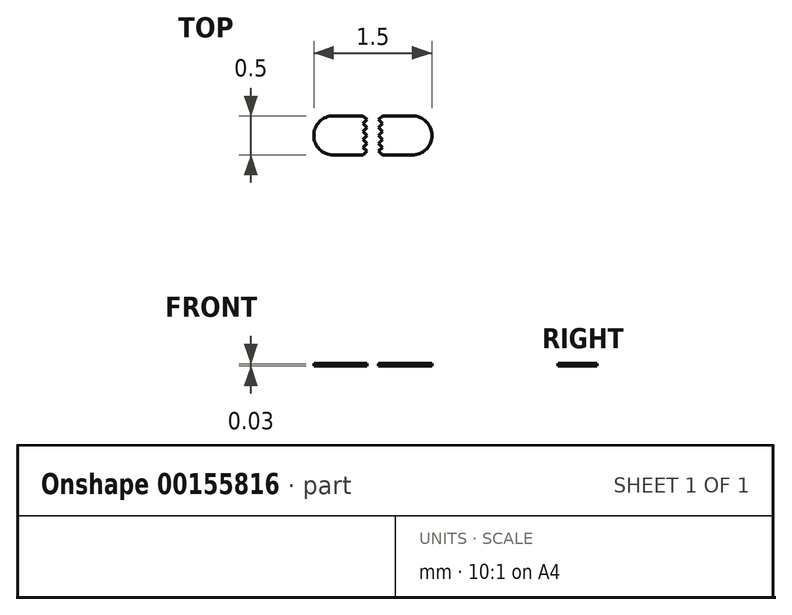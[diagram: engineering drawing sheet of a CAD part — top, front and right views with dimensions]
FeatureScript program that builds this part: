
annotation { "Feature Type Name" : "Feature", "Feature Type Description" : "" }
export const myFeature = defineFeature(function(context is Context, id is Id, definition is map)
    precondition{}
    {
        {
            var Q0;
            Q0=qCreatedBy(makeId("Top.planeOp"),FACE);
            var sketch = newSketch(context, id + "F0", { "sketchPlane" : qUnion([Q0])});
            skArc(sketch, "E0", {"start": v(-0.5, 0.25) * mm, "mid": v(-0.75, 0) * mm, "end": v(-0.5, -0.25) * mm});
            skLineSegment(sketch, "E1.bottom", {"start": v(-0.5, 0.25) * mm, "end": v(-0.13, 0.25) * mm});
            skLineSegment(sketch, "E1.top", {"start": v(-0.5, -0.25) * mm, "end": v(-0.12, -0.25) * mm});
            skLineSegment(sketch, "E2", {"start": v(-0.13, 0.25) * mm, "end": v(-0.08, 0.2) * mm});
            skLineSegment(sketch, "E3.MirrorCS", {"start": v(-0.13, 0.15) * mm, "end": v(-0.08, 0.2) * mm});
            skLineSegment(sketch, "E4.MirrorCS", {"start": v(-0.13, 0.15) * mm, "end": v(-0.08, 0.1) * mm});
            skLineSegment(sketch, "E5.MirrorCS", {"start": v(-0.13, 0.05) * mm, "end": v(-0.08, 0.1) * mm});
            skLineSegment(sketch, "E6", {"start": v(-0.12, 0.05) * mm, "end": v(-0.08, 0) * mm});
            skLineSegment(sketch, "E7.MirrorCS", {"start": v(-0.12, -0.05) * mm, "end": v(-0.08, 0) * mm});
            skLineSegment(sketch, "E8.MirrorCS", {"start": v(-0.13, -0.05) * mm, "end": v(-0.08, -0.1) * mm});
            skLineSegment(sketch, "E9.MirrorCS", {"start": v(-0.13, -0.15) * mm, "end": v(-0.08, -0.1) * mm});
            skLineSegment(sketch, "E10.MirrorCS", {"start": v(-0.13, -0.15) * mm, "end": v(-0.08, -0.2) * mm});
            skLineSegment(sketch, "E11.MirrorCS", {"start": v(-0.12, -0.25) * mm, "end": v(-0.07, -0.2) * mm});
            skPoint(sketch, "E12.center.orphan", {"position": v(0.5, 0) * mm});
            skLineSegment(sketch, "E13.MirrorCS", {"start": v(0.13, 0.05) * mm, "end": v(0.08, 0.1) * mm});
            skLineSegment(sketch, "E14.MirrorCS", {"start": v(0.13, -0.25) * mm, "end": v(0.08, -0.2) * mm});
            skLineSegment(sketch, "E15.MirrorCS", {"start": v(0.12, -0.05) * mm, "end": v(0.08, 0) * mm});
            skLineSegment(sketch, "E16.MirrorCS", {"start": v(0.13, 0.15) * mm, "end": v(0.08, 0.2) * mm});
            skLineSegment(sketch, "E17.MirrorCS", {"start": v(0.13, -0.15) * mm, "end": v(0.08, -0.1) * mm});
            skLineSegment(sketch, "E18.MirrorCS", {"start": v(0.5, -0.25) * mm, "end": v(0.12, -0.25) * mm});
            skLineSegment(sketch, "E19.MirrorCS", {"start": v(0.12, 0.05) * mm, "end": v(0.08, 0) * mm});
            skLineSegment(sketch, "E20.MirrorCS", {"start": v(0.5, 0.25) * mm, "end": v(0.13, 0.25) * mm});
            skLineSegment(sketch, "E21.MirrorCS", {"start": v(0.13, 0.25) * mm, "end": v(0.08, 0.2) * mm});
            skLineSegment(sketch, "E22.MirrorCS", {"start": v(0.13, -0.15) * mm, "end": v(0.08, -0.2) * mm});
            skLineSegment(sketch, "E23.MirrorCS", {"start": v(0.13, 0.15) * mm, "end": v(0.08, 0.1) * mm});
            skLineSegment(sketch, "E24.MirrorCS", {"start": v(0.13, -0.05) * mm, "end": v(0.08, -0.1) * mm});
            skArc(sketch, "E25.MirrorCS", {"start": v(0.5, 0.25) * mm, "mid": v(0.75, 0) * mm, "end": v(0.5, -0.25) * mm});
            skSolve(sketch);
        }
        {
            var Q0;
            Q0=makeQuery(id+"F0.imprint","IMPRINT",FACE,{"disambiguationData":[TD([[makeQuery(id+"F0.imprint","IMPRINT",EDGE,{"derivedFrom":sQuery(id+"F0.wireOp",EDGE,"E0")}),1.0]])]});
            var Q1;
            Q1=makeQuery(id+"F0.imprint","IMPRINT",FACE,{"disambiguationData":[TD([[makeQuery(id+"F0.imprint","IMPRINT",EDGE,{"derivedFrom":sQuery(id+"F0.wireOp",EDGE,"E13.MirrorCS")}),-1.0]])]});
            extrude(context, id + "F1", {"entities" : qUnion([Q0, Q1]), "depth" : 0.04 * mm});
        }
    });
